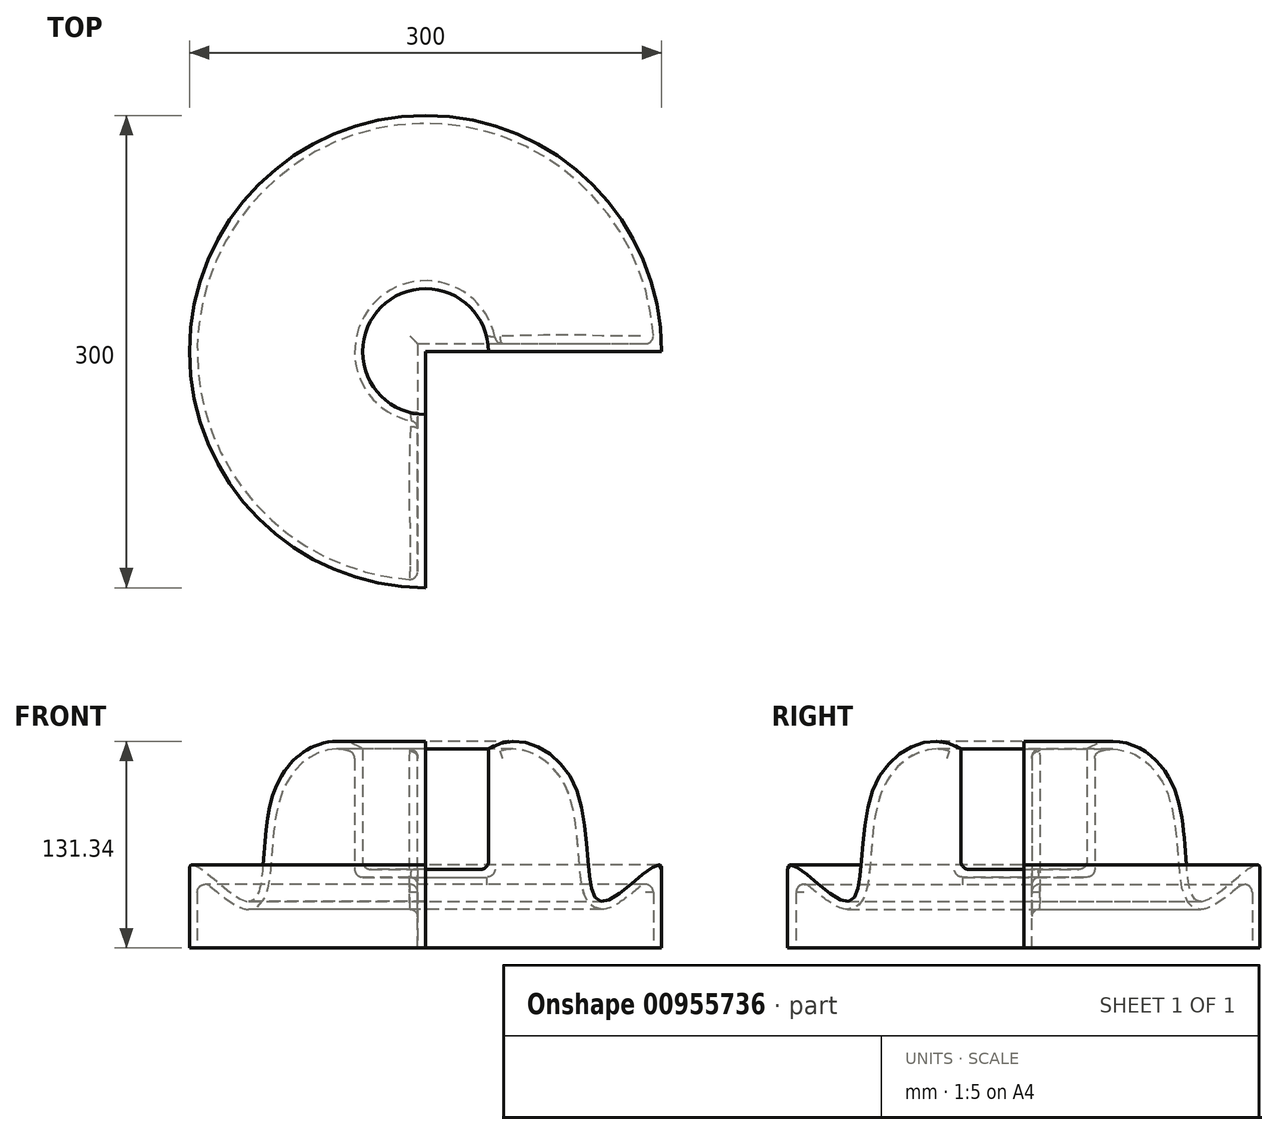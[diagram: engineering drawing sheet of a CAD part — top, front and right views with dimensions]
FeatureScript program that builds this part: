
annotation { "Feature Type Name" : "Feature", "Feature Type Description" : "" }
export const myFeature = defineFeature(function(context is Context, id is Id, definition is map)
    precondition{}
    {
        {
            var Q0;
            Q0=qCreatedBy(makeId("Front.planeOp"),FACE);
            var sketch = newSketch(context, id + "F0", { "sketchPlane" : qUnion([Q0])});
            skLineSegment(sketch, "E0.bottom", {"start": v(0, 0) * mm, "end": v(150, 0) * mm});
            skLineSegment(sketch, "E0.top", {"start": v(0, 50) * mm, "end": v(40, 50) * mm});
            skLineSegment(sketch, "E0.left", {"start": v(0, 0) * mm, "end": v(0, 50) * mm});
            skLineSegment(sketch, "E0.right", {"start": v(150, 0) * mm, "end": v(150, 50) * mm});
            skLineSegment(sketch, "E1", {"start": v(40, 50) * mm, "end": v(40, 126.59) * mm});
            skFitSpline(sketch, "E2", {"points": [v(40, 126.59) * mm, v(95.58, 101.17) * mm, v(113.8, 29.76) * mm, v(150, 50) * mm], "startDerivative": vector(164.39, 104.97) * mm, "endDerivative": vector(0, -128.53) * mm});
            skSolve(sketch);
        }
        {
            var Q0;
            Q0=makeQuery(id+"F0.imprint","IMPRINT",FACE,{"disambiguationData":[TD([[makeQuery(id+"F0.imprint","IMPRINT",EDGE,{"derivedFrom":sQuery(id+"F0.wireOp",EDGE,"E0.bottom")}),1.0]])]});
            var Q1;
            Q1=sQuery(id+"F0.wireOp",EDGE,"E0.left");
            revolve(context, id + "F1", {"surfaceOperationType" : NewSurfaceOperationType.NEW, "entities" : qUnion([Q0]), "axis" : qUnion([Q1]), "revolveType" : RevolveType.ONE_DIRECTION, "angle" : 270 * degree});
        }
        {
            var Q0;
            Q0=makeQuery(id+"F1.opRevolve","SWEPT_FACE",FACE,{"disambiguationData":[OSD([sQuery(id+"F0.wireOp",EDGE,"E0.bottom")])]});
            var Q1;
            Q1=makeQuery(id+"F1.opRevolve","SWEPT_BODY",BODY,{"disambiguationData":[OSD([sQuery(id+"F0.wireOp",EDGE,"E0.bottom"),sQuery(id+"F0.wireOp",EDGE,"E0.top"),sQuery(id+"F0.wireOp",EDGE,"E0.left"),sQuery(id+"F0.wireOp",EDGE,"E0.right"),sQuery(id+"F0.wireOp",EDGE,"E1"),sQuery(id+"F0.wireOp",EDGE,"E2")])]});
            shell(context, id + "F2", {"entities" : qUnion([Q0]), "parts" : qUnion([Q1]), "thickness" : 5 * mm});
        }
        {
            var Q0;
            Q0=makeQuery(id+"F1.opRevolve","SWEPT_EDGE",EDGE,{"disambiguationData":[OSD([sQuery(id+"F0.wireOp",EDGE,"E0.top"),sQuery(id+"F0.wireOp",EDGE,"E1")])]});
            fillet(context, id + "F3", {"entities" : qUnion([Q0]), "radius" : 5 * mm, "tangentPropagation" : true, "allowEdgeOverflow" : false});
        }
        {
            var Q0;
            Q0=makeQuery(id+"F2.opShell","OFFSET_EDGE",EDGE,{"disambiguationData":[OSD([sQuery(id+"F0.wireOp",EDGE,"E0.top"),sQuery(id+"F0.wireOp",EDGE,"E1")])]});
            fillet(context, id + "F4", {"entities" : qUnion([Q0]), "radius" : 5 * mm, "tangentPropagation" : true, "allowEdgeOverflow" : false});
        }
        {
            var Q0;
            {var subQ0=sQuery(id+"F0.wireOp",EDGE,"E0.right");Q0=makeQuery(id+"F2.opShell","OFFSET_EDGE",EDGE,{"disambiguationData":[OSD([subQ0]),TDD([makeQuery(id+"F1.opRevolve","CAP_EDGE",EDGE,{"disambiguationData":[OSD([subQ0])],"isStart":false})])]});}
            var Q1;
            {var subQ0=sQuery(id+"F0.wireOp",EDGE,"E0.right");Q1=makeQuery(id+"F2.opShell","OFFSET_EDGE",EDGE,{"disambiguationData":[OSD([subQ0]),TDD([makeQuery(id+"F1.opRevolve","CAP_EDGE",EDGE,{"disambiguationData":[OSD([subQ0])],"isStart":true})])]});}
            fillet(context, id + "F5", {"entities" : qUnion([Q0, Q1]), "radius" : 5 * mm, "tangentPropagation" : true, "allowEdgeOverflow" : false});
        }
        {
            var Q0;
            {var subQ0=sQuery(id+"F0.wireOp",EDGE,"E2");Q0=makeQuery(id+"F2.opShell","OFFSET_EDGE",EDGE,{"disambiguationData":[OSD([subQ0]),TDD([makeQuery(id+"F1.opRevolve","CAP_EDGE",EDGE,{"disambiguationData":[OSD([subQ0])],"isStart":false})])]});}
            var Q1;
            {var subQ0=sQuery(id+"F0.wireOp",EDGE,"E1");Q1=makeQuery(id+"F2.opShell","OFFSET_EDGE",EDGE,{"disambiguationData":[OSD([subQ0]),TDD([makeQuery(id+"F1.opRevolve","CAP_EDGE",EDGE,{"disambiguationData":[OSD([subQ0])],"isStart":false})])]});}
            var Q2;
            {var subQ0=sQuery(id+"F0.wireOp",EDGE,"E1");var subQ1=sQuery(id+"F0.wireOp",EDGE,"E0.top");Q2=makeQuery(id+"F4.opFillet","BLEND_EDGE",EDGE,{"disambiguationData":[OD(1.0)],"blendedFrom":[makeQuery(id+"F2.opShell","OFFSET_EDGE",EDGE,{"disambiguationData":[OSD([subQ1,subQ0])]}),makeQuery(id+"F2.opShell","OFFSET_FACE",FACE,{"disambiguationData":[OSD([sQuery(id+"F0.wireOp",EDGE,"E0.bottom"),subQ1,sQuery(id+"F0.wireOp",EDGE,"E0.left"),sQuery(id+"F0.wireOp",EDGE,"E0.right"),subQ0,sQuery(id+"F0.wireOp",EDGE,"E2")])]})],"blendedInto":[makeQuery(id+"F2.opShell","OFFSET_FACE",FACE,{"disambiguationData":[OSD([sQuery(id+"F0.wireOp",EDGE,"E0.bottom"),subQ1,sQuery(id+"F0.wireOp",EDGE,"E0.left"),sQuery(id+"F0.wireOp",EDGE,"E0.right"),subQ0,sQuery(id+"F0.wireOp",EDGE,"E2")])]})]});}
            var Q3;
            Q3=makeQuery(id+"F2.opShell","OFFSET_EDGE",EDGE,{"disambiguationData":[OSD([sQuery(id+"F0.wireOp",EDGE,"E0.top")])]});
            var Q4;
            {var subQ0=sQuery(id+"F0.wireOp",EDGE,"E1");var subQ1=sQuery(id+"F0.wireOp",EDGE,"E0.top");Q4=makeQuery(id+"F4.opFillet","BLEND_EDGE",EDGE,{"disambiguationData":[OD(0.0)],"blendedFrom":[makeQuery(id+"F2.opShell","OFFSET_EDGE",EDGE,{"disambiguationData":[OSD([subQ1,subQ0])]}),makeQuery(id+"F2.opShell","OFFSET_FACE",FACE,{"disambiguationData":[OSD([sQuery(id+"F0.wireOp",EDGE,"E0.bottom"),subQ1,sQuery(id+"F0.wireOp",EDGE,"E0.left"),sQuery(id+"F0.wireOp",EDGE,"E0.right"),subQ0,sQuery(id+"F0.wireOp",EDGE,"E2")])]})],"blendedInto":[makeQuery(id+"F2.opShell","OFFSET_FACE",FACE,{"disambiguationData":[OSD([sQuery(id+"F0.wireOp",EDGE,"E0.bottom"),subQ1,sQuery(id+"F0.wireOp",EDGE,"E0.left"),sQuery(id+"F0.wireOp",EDGE,"E0.right"),subQ0,sQuery(id+"F0.wireOp",EDGE,"E2")])]})]});}
            var Q5;
            {var subQ0=sQuery(id+"F0.wireOp",EDGE,"E1");Q5=makeQuery(id+"F2.opShell","OFFSET_EDGE",EDGE,{"disambiguationData":[OSD([subQ0]),TDD([makeQuery(id+"F1.opRevolve","CAP_EDGE",EDGE,{"disambiguationData":[OSD([subQ0])],"isStart":true})])]});}
            var Q6;
            {var subQ0=sQuery(id+"F0.wireOp",EDGE,"E2");Q6=makeQuery(id+"F2.opShell","OFFSET_EDGE",EDGE,{"disambiguationData":[OSD([subQ0]),TDD([makeQuery(id+"F1.opRevolve","CAP_EDGE",EDGE,{"disambiguationData":[OSD([subQ0])],"isStart":true})])]});}
            fillet(context, id + "F6", {"entities" : qUnion([Q0, Q1, Q2, Q3, Q4, Q5, Q6]), "radius" : 5 * mm, "tangentPropagation" : true, "allowEdgeOverflow" : false});
        }
        {
            var Q0;
            Q0=makeQuery(id+"F2.opShell","OFFSET_EDGE",EDGE,{"disambiguationData":[OSD([sQuery(id+"F0.wireOp",EDGE,"E1"),sQuery(id+"F0.wireOp",EDGE,"E2")])]});
            fillet(context, id + "F7", {"entities" : qUnion([Q0]), "radius" : 5 * mm, "tangentPropagation" : true, "allowEdgeOverflow" : false});
        }
    });
